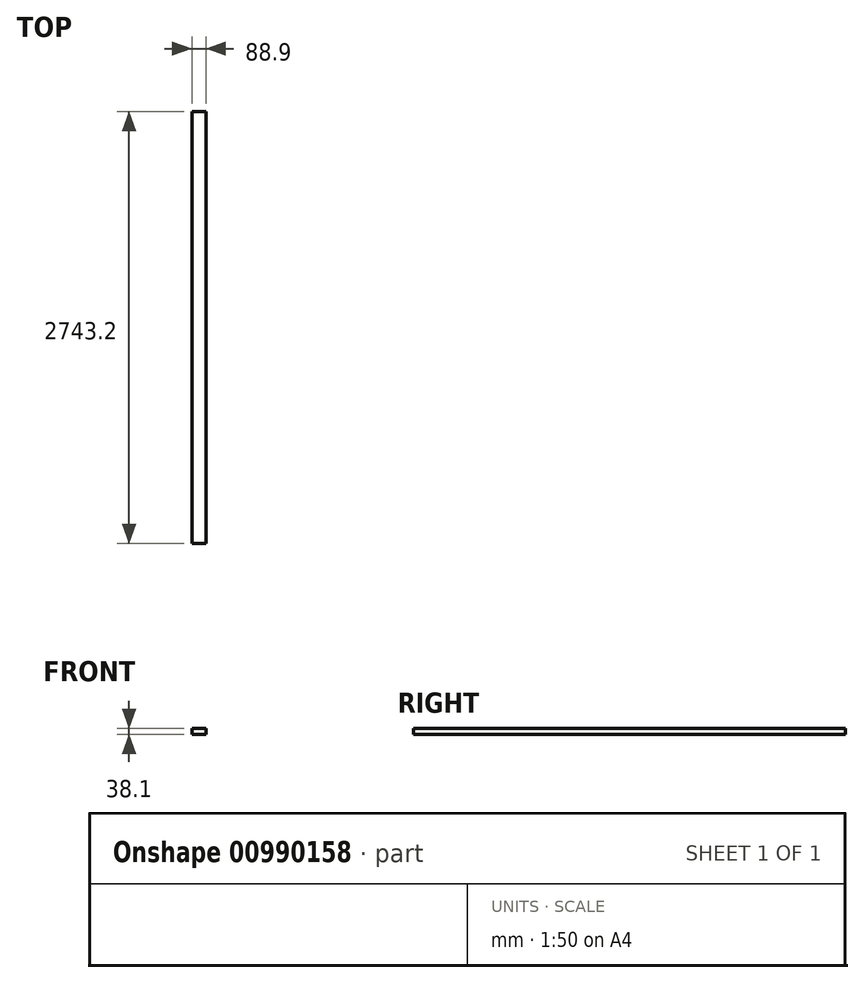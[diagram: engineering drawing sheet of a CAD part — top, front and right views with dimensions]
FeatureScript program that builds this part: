
annotation { "Feature Type Name" : "Feature", "Feature Type Description" : "" }
export const myFeature = defineFeature(function(context is Context, id is Id, definition is map)
    precondition{}
    {
        {
            assignVariable(context, id + "F0", {"name" : "w", "anyValue" : 38.1 * mm});
        }
        {
            var Q0;
            Q0=qCreatedBy(makeId("Top.planeOp"),FACE);
            var sketch = newSketch(context, id + "F1", { "sketchPlane" : qUnion([Q0])});
            skLineSegment(sketch, "E0.bottom", {"start": v(44.45, 1371.6) * mm, "end": v(-44.45, 1371.6) * mm});
            skLineSegment(sketch, "E0.top", {"start": v(44.45, -1371.6) * mm, "end": v(-44.45, -1371.6) * mm});
            skLineSegment(sketch, "E0.left", {"start": v(44.45, 1371.6) * mm, "end": v(44.45, -1371.6) * mm});
            skLineSegment(sketch, "E0.right", {"start": v(-44.45, 1371.6) * mm, "end": v(-44.45, -1371.6) * mm});
            skPoint(sketch, "E0.middle", {"position": v(0, 0) * mm});
            skSolve(sketch);
        }
        {
            var Q0;
            Q0 = qSketchRegion(id + "F1", true);
            extrude(context, id + "F2", {"entities" : qUnion([Q0]), "depth" : getVariable(context, 'w'), "offsetDistance" : 25.4 * mm});
        }
    });
